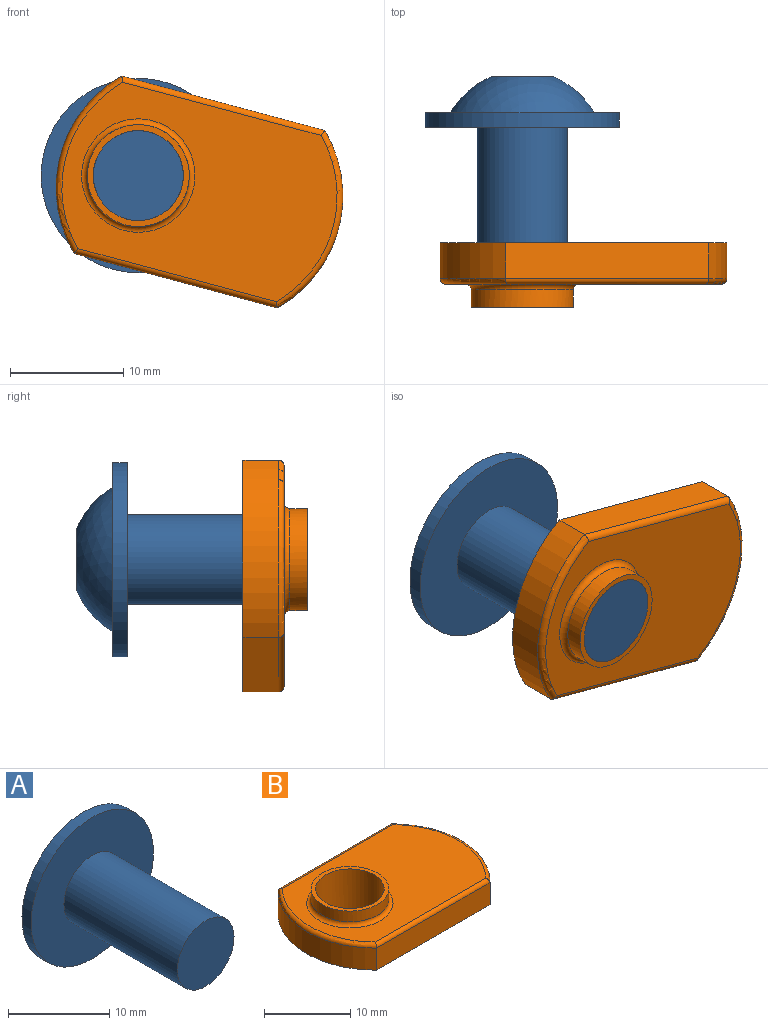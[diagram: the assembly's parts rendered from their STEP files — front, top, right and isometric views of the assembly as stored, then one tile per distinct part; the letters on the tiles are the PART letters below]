
ASSEMBLY  parts=2 mates=1
PART A: 19 faces, bbox 17.1x20.9x17.1 mm
  f0: sphere r=7.28mm, area 145.3mm2, adj f3,f4,f5,f6,f7,f10,f11
  f1: cylinder r=8.57mm len=17.15mm, axis (0,-1,0), area 68.4mm2, adj f9,f10
  f2: cylinder r=3.97mm len=15.88mm, axis (0,-1,0), area 395.9mm2, adj f8,f9
  f3: plane 2.39x1.38mm, normal (0,1,0), area 0.7mm2, adj f0,f12
  f4: plane 2.76x0.37mm, normal (0,1,0), area 0.7mm2, adj f0,f13
  f5: plane 2.39x1.38mm, normal (0,1,0), area 0.7mm2, adj f0,f14
  f6: plane 2.39x1.38mm, normal (0,1,0), area 0.7mm2, adj f0,f15
  f7: plane 2.76x0.37mm, normal (0,1,0), area 0.7mm2, adj f0,f16
  f8: plane 7.94x7.94mm, normal (0,-1,0), area 49.5mm2, adj f2
  f9: plane 17.15x17.15mm, normal (0,-1,0), area 181.4mm2, adj f1,f2
  f10: plane 17.15x17.15mm, normal (0,1,0), area 104.2mm2, adj f0,f1
  f11: plane 2.39x1.38mm, normal (0,1,0), area 0.7mm2, adj f0,f17
  f12: plane 3.18x2.39mm, normal (-0.87,0,-0.5), area 8.8mm2, adj f3,f13,f17,f18
  f13: plane 3.18x2.76mm, normal (0,0,-1), area 8.8mm2, adj f4,f12,f14,f18
  f14: plane 3.18x2.39mm, normal (0.87,0,-0.5), area 8.8mm2, adj f5,f13,f15,f18
  f15: plane 3.18x2.39mm, normal (0.87,0,0.5), area 8.8mm2, adj f6,f14,f16,f18
  f16: plane 3.18x2.76mm, normal (0,0,1), area 8.8mm2, adj f7,f15,f17,f18
  f17: plane 3.18x2.39mm, normal (-0.87,0,0.5), area 8.8mm2, adj f11,f12,f16,f18
  f18: plane 5.51x4.78mm, normal (0,1,0), area 19.7mm2, adj f12,f13,f14,f15,f16,f17
PART B: 14 faces, bbox 27.3x17.5x5.7 mm
  f0: torus R=5mm, axis (0,0,-1), area 23.5mm2, adj f4,f6
  f1: torus R=10.78mm, axis (0,0,-1), area 14mm2, adj f2,f6,f11,f13
  f2: cylinder r=11.29mm len=16.21mm, axis (0,0,-1), area 56.5mm2, adj f1,f5,f7,f8
  f3: cylinder r=3.97mm len=7.94mm, axis (0,0,1), area 141.2mm2, adj f5,f9
  f4: cylinder r=4.5mm len=8.99mm, axis (0,0,-1), area 43mm2, adj f0,f9
  f5: plane 25.4x16.21mm, normal (0,0,-1), area 327.7mm2, adj f2,f3,f7,f8,f10
  f6: plane 24.38x15.19mm, normal (0,0,1), area 262.1mm2, adj f0,f1,f11,f12,f13
  f7: plane 18.54x3.12mm, normal (0,1,0), area 57.9mm2, adj f2,f5,f10,f13
  f8: plane 18.54x3.12mm, normal (0,-1,0), area 57.9mm2, adj f2,f5,f10,f11
  f9: plane 8.99x8.99mm, normal (0,0,1), area 14mm2, adj f3,f4
  f10: cylinder r=11.29mm len=16.21mm, axis (0,0,-1), area 56.5mm2, adj f5,f7,f8,f12
  f11: cylinder r=0.51mm len=18.54mm, axis (-1,0,0), area 14.6mm2, adj f1,f6,f8,f12
  f12: torus R=10.78mm, axis (0,0,-1), area 14mm2, adj f6,f10,f11,f13
  f13: cylinder r=0.51mm len=18.54mm, axis (1,0,0), area 14.6mm2, adj f1,f6,f7,f12
PLACE A rot(axis=(0,1,0),15deg) t=(-268.16,-55.22,2.54)mm
PLACE B rot(axis=(0.98,0.13,-0.13),91deg) t=(-277.13,-53.19,-3.44)mm
MATE fastened A.f1 <-> B.f0  axis (0,-1,0) through (-268.16,-55.22,2.54)mm
